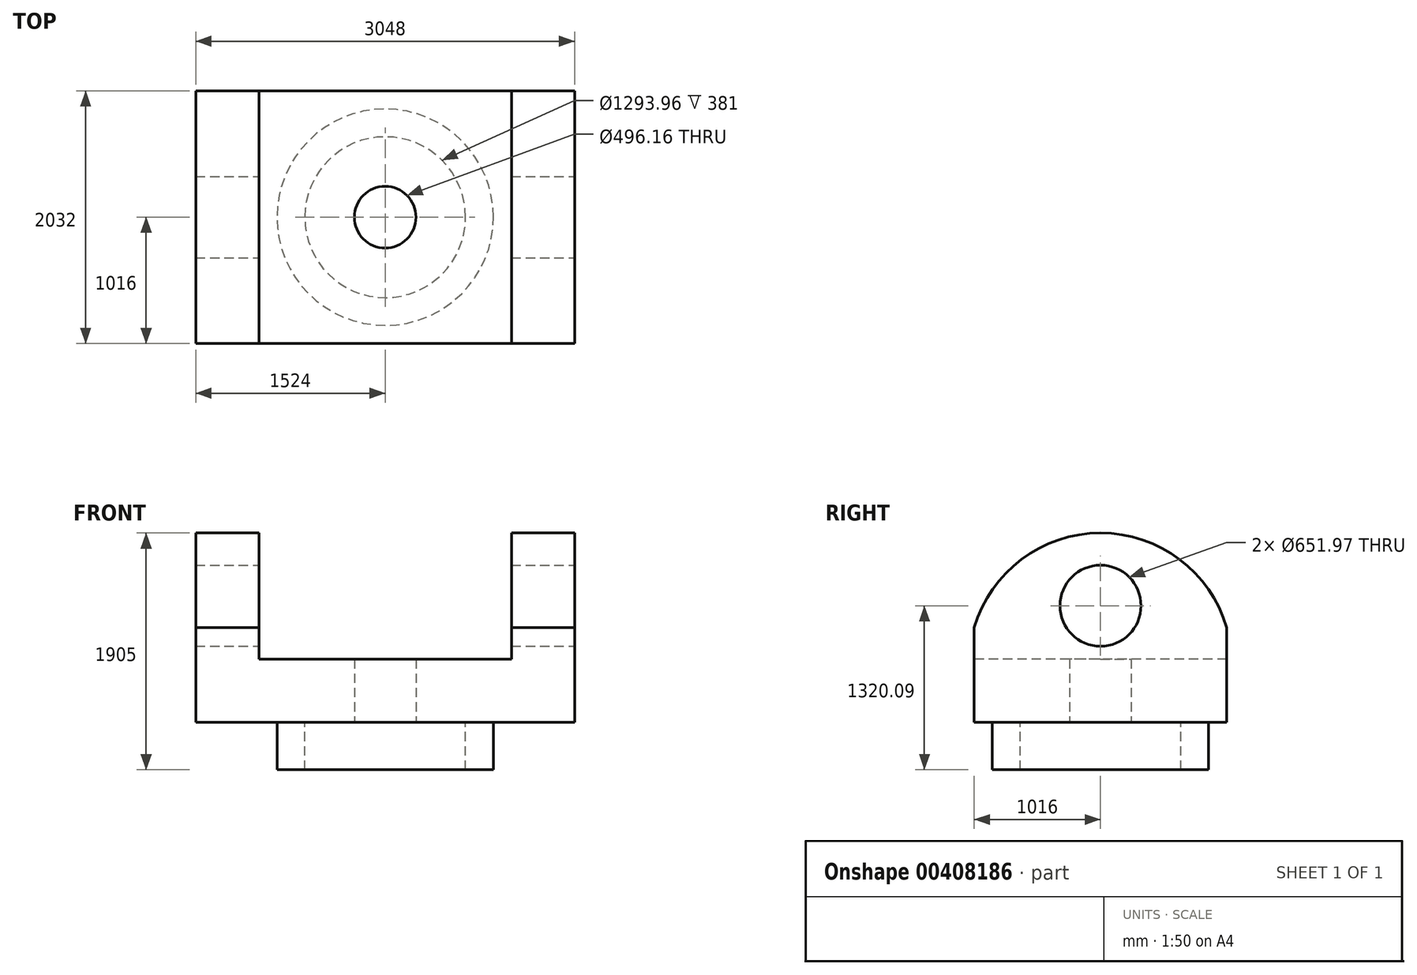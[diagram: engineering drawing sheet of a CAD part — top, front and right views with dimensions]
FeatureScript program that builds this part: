
annotation { "Feature Type Name" : "Feature", "Feature Type Description" : "" }
export const myFeature = defineFeature(function(context is Context, id is Id, definition is map)
    precondition{}
    {
        {
            var Q0;
            Q0=qCreatedBy(makeId("Top.planeOp"),FACE);
            var sketch = newSketch(context, id + "F0", { "sketchPlane" : qUnion([Q0])});
            skLineSegment(sketch, "E0.bottom", {"start": v(-1524, -1016) * mm, "end": v(1524, -1016) * mm});
            skLineSegment(sketch, "E0.top", {"start": v(-1524, 1016) * mm, "end": v(1524, 1016) * mm});
            skLineSegment(sketch, "E0.left", {"start": v(-1524, -1016) * mm, "end": v(-1524, 1016) * mm});
            skLineSegment(sketch, "E0.right", {"start": v(1524, -1016) * mm, "end": v(1524, 1016) * mm});
            skPoint(sketch, "E0.middle", {"position": v(0, 0) * mm});
            skSolve(sketch);
        }
        {
            var Q0;
            Q0 = qSketchRegion(id + "F0", true);
            extrude(context, id + "F1", {"entities" : qUnion([Q0]), "depth" : 1524 * mm});
        }
        {
            var Q0;
            Q0=makeQuery(id+"F1.opExtrude","SWEPT_FACE",FACE,{"disambiguationData":[OSD([sQuery(id+"F0.wireOp",EDGE,"E0.right")])]});
            var sketch = newSketch(context, id + "F2", { "sketchPlane" : qUnion([Q0])});
            skArc(sketch, "E1", {"start": v(1016, 762) * mm, "mid": v(0, 1524) * mm, "end": v(-1016, 762) * mm});
            skLineSegment(sketch, "E2", {"start": v(-1016, 762) * mm, "end": v(-1016, 1524) * mm});
            skLineSegment(sketch, "E3", {"start": v(-1016, 1524) * mm, "end": v(1016, 1524) * mm});
            skLineSegment(sketch, "E4", {"start": v(1016, 1524) * mm, "end": v(1016, 762) * mm});
            skSolve(sketch);
        }
        {
            var Q0;
            {var subQ0=sQuery(id+"F2.wireOp",EDGE,"E4");Q0=makeQuery(id+"F2.imprint","IMPRINT",FACE,{"disambiguationData":[TD([[makeQuery(id+"F2.imprint","IMPRINT",EDGE,{"derivedFrom":subQ0}),-1.0]])]});}
            var Q1;
            {var subQ0=sQuery(id+"F2.wireOp",EDGE,"E2");Q1=makeQuery(id+"F2.imprint","IMPRINT",FACE,{"disambiguationData":[TD([[makeQuery(id+"F2.imprint","IMPRINT",EDGE,{"derivedFrom":subQ0}),1.0]])]});}
            extrude(context, id + "F3", {"entities" : qUnion([Q0, Q1]), "operationType" : NewBodyOperationType.REMOVE, "endBound" : BoundingType.THROUGH_ALL, "oppositeDirection" : true, "depth" : 25.4 * mm});
        }
        {
            var Q0;
            Q0=qCreatedBy(makeId("Front.planeOp"),FACE);
            cPlane(context, id + "F4", {"entities" : qUnion([Q0]), "cplaneType" : CPlaneType.OFFSET, "offset" : 1117.6 * mm, "width" : 152.4 * mm, "height" : 152.4 * mm});
        }
        {
            var Q0;
            Q0=qCreatedBy(id+"F4.planeOp",FACE);
            var sketch = newSketch(context, id + "F5", { "sketchPlane" : qUnion([Q0])});
            skLineSegment(sketch, "E5.bottom", {"start": v(1016, 1823.52) * mm, "end": v(-1016, 1823.52) * mm});
            skLineSegment(sketch, "E5.top", {"start": v(1016, 508) * mm, "end": v(-1016, 508) * mm});
            skLineSegment(sketch, "E5.left", {"start": v(1016, 1823.52) * mm, "end": v(1016, 508) * mm});
            skLineSegment(sketch, "E5.right", {"start": v(-1016, 1823.52) * mm, "end": v(-1016, 508) * mm});
            skSolve(sketch);
        }
        {
            var Q0;
            Q0 = qSketchRegion(id + "F5", true);
            extrude(context, id + "F6", {"entities" : qUnion([Q0]), "operationType" : NewBodyOperationType.REMOVE, "endBound" : BoundingType.THROUGH_ALL, "oppositeDirection" : true, "depth" : 25.4 * mm});
        }
        {
            var Q0;
            Q0=qCreatedBy(makeId("Top.planeOp"),FACE);
            var sketch = newSketch(context, id + "F7", { "sketchPlane" : qUnion([Q0])});
            skCircle(sketch, "E6", {"center": v(0, 0) * mm, "radius": 870.4 * mm});
            skCircle(sketch, "E7", {"center": v(0, 0) * mm, "radius": 646.98 * mm});
            skSolve(sketch);
        }
        {
            var Q0;
            Q0 = qSketchRegion(id + "F7", true);
            extrude(context, id + "F8", {"entities" : qUnion([Q0]), "operationType" : NewBodyOperationType.ADD, "oppositeDirection" : true, "depth" : 381 * mm});
        }
        {
            var Q0;
            Q0=makeQuery(id+"F8.boolean.opBoolean","SPLIT",FACE,{"disambiguationData":[TD([makeQuery(id+"F8.opExtrude","SWEPT_FACE",FACE,{"disambiguationData":[OSD([sQuery(id+"F7.wireOp",EDGE,"E7")])]})])],"derivedFrom":makeQuery(id+"F1.opExtrude","CAP_FACE",FACE,{"disambiguationData":[OSD([sQuery(id+"F0.wireOp",EDGE,"E0.bottom"),sQuery(id+"F0.wireOp",EDGE,"E0.top"),sQuery(id+"F0.wireOp",EDGE,"E0.left"),sQuery(id+"F0.wireOp",EDGE,"E0.right")])],"isStart":true})});
            var sketch = newSketch(context, id + "F9", { "sketchPlane" : qUnion([Q0])});
            skCircle(sketch, "E8", {"center": v(0, 0) * mm, "radius": 248.08 * mm});
            skSolve(sketch);
        }
        {
            var Q0;
            Q0=makeQuery(id+"F9.imprint","IMPRINT",FACE,{"disambiguationData":[TD([[makeQuery(id+"F9.imprint","IMPRINT",EDGE,{"derivedFrom":sQuery(id+"F9.wireOp",EDGE,"E8")}),1.0]])]});
            extrude(context, id + "F10", {"entities" : qUnion([Q0]), "operationType" : NewBodyOperationType.REMOVE, "oppositeDirection" : true, "depth" : 1734.82 * mm});
        }
        {
            var Q0;
            Q0=qCreatedBy(makeId("Right.planeOp"),FACE);
            var sketch = newSketch(context, id + "F11", { "sketchPlane" : qUnion([Q0])});
            skCircle(sketch, "E9", {"center": v(0, 939.09) * mm, "radius": 325.99 * mm});
            skSolve(sketch);
        }
        {
            var Q0;
            Q0 = qSketchRegion(id + "F11", true);
            extrude(context, id + "F12", {"entities" : qUnion([Q0]), "operationType" : NewBodyOperationType.REMOVE, "oppositeDirection" : true, "depth" : 1981.2 * mm, "hasSecondDirection" : true, "secondDirectionOppositeDirection" : false, "secondDirectionDepth" : 1854.2 * mm});
        }
    });
